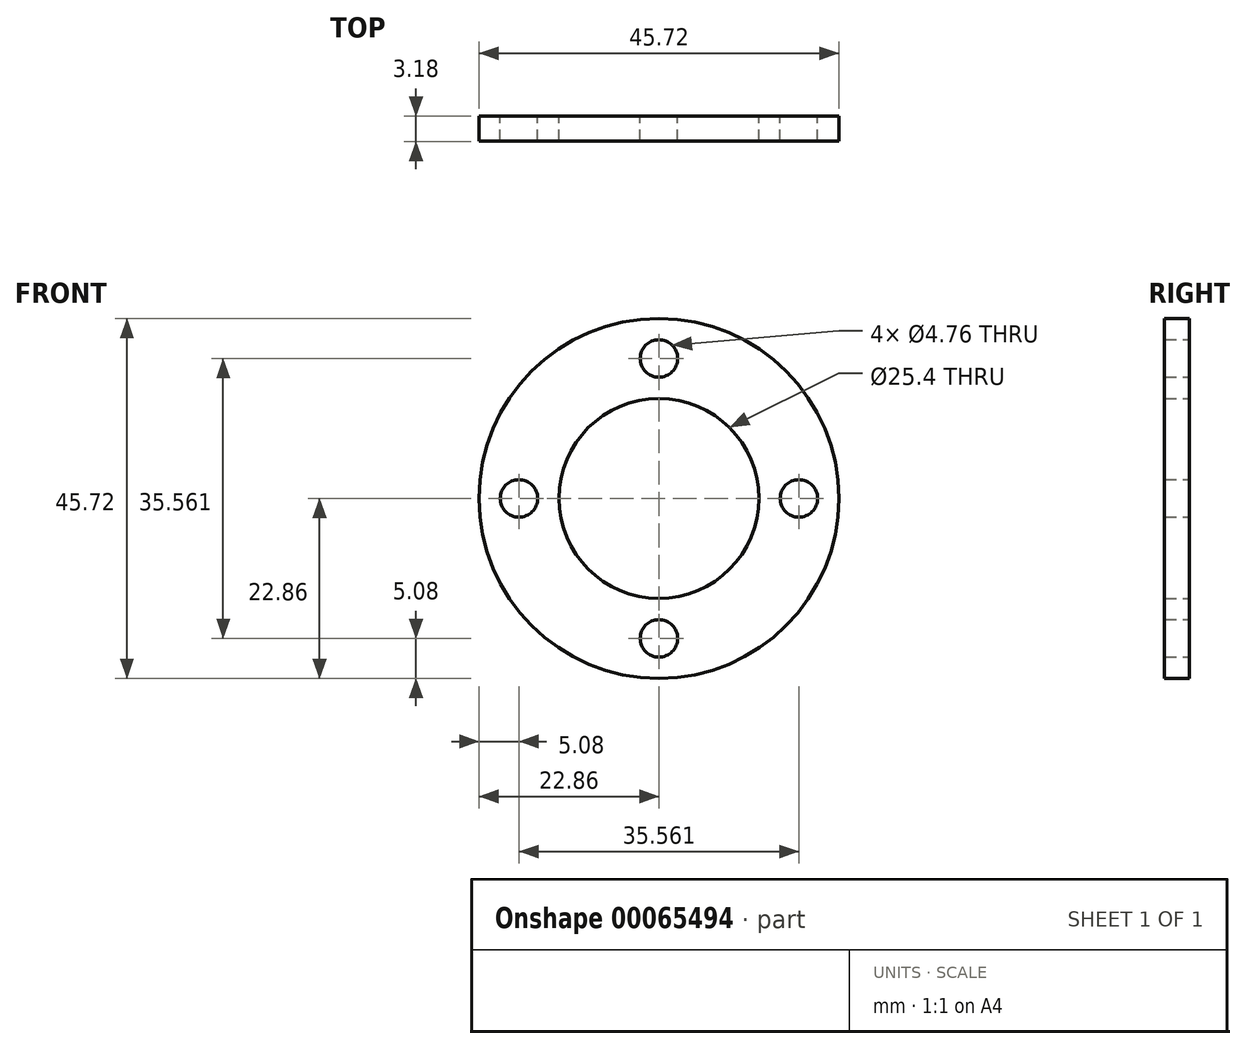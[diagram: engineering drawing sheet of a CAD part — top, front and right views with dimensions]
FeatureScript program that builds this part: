
annotation { "Feature Type Name" : "Feature", "Feature Type Description" : "" }
export const myFeature = defineFeature(function(context is Context, id is Id, definition is map)
    precondition{}
    {
        {
            var Q0;
            Q0=qCreatedBy(makeId("Front.planeOp"),FACE);
            var sketch = newSketch(context, id + "F0", { "sketchPlane" : qUnion([Q0])});
            skCircle(sketch, "E0", {"center": v(0, 0) * mm, "radius": 22.86 * mm});
            skCircle(sketch, "E1", {"center": v(0, 0) * mm, "radius": 12.7 * mm});
            skLineSegment(sketch, "E2", {"start": v(-22.86, 0) * mm, "end": v(-12.7, 0) * mm});
            skCircle(sketch, "E3", {"center": v(-17.78, 0) * mm, "radius": 2.38 * mm});
            skCircle(sketch, "E4.1.0", {"center": v(0, -17.78) * mm, "radius": 2.38 * mm});
            skCircle(sketch, "E4.2.0", {"center": v(17.78, 0) * mm, "radius": 2.38 * mm});
            skCircle(sketch, "E4.3.0", {"center": v(0, 17.78) * mm, "radius": 2.38 * mm});
            skSolve(sketch);
        }
        {
            var Q0;
            Q0=makeQuery(id+"F0.imprint","IMPRINT",FACE,{"disambiguationData":[TD([[makeQuery(id+"F0.imprint","IMPRINT",EDGE,{"derivedFrom":sQuery(id+"F0.wireOp",EDGE,"E0")}),1.0]])]});
            extrude(context, id + "F1", {"entities" : qUnion([Q0]), "depth" : 3.17 * mm});
        }
    });
